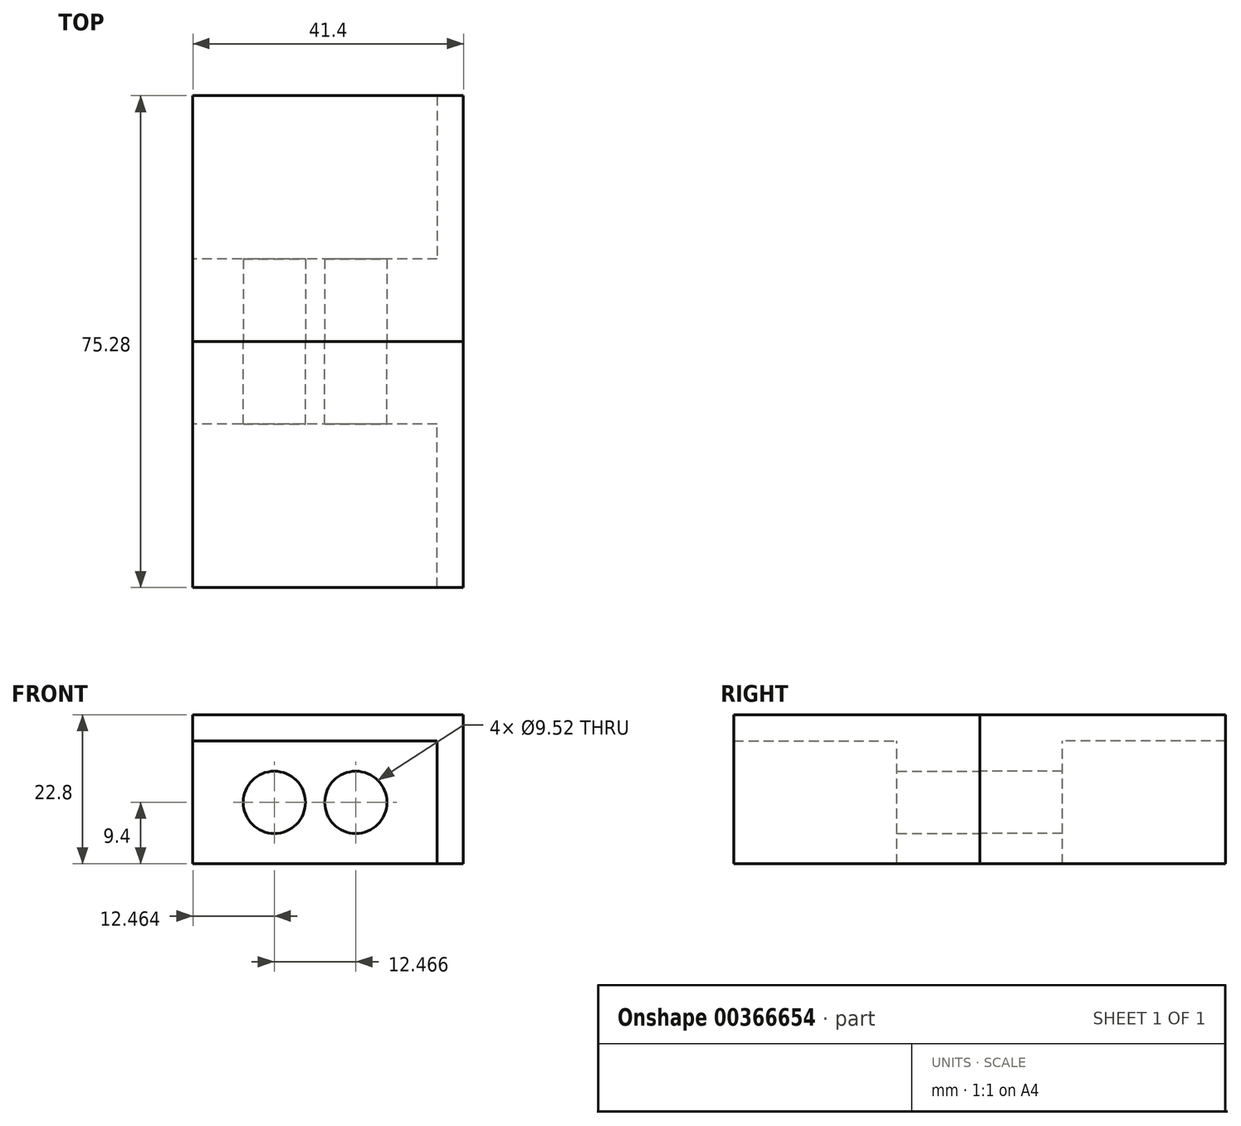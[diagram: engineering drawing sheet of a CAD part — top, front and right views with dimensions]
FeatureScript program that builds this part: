
annotation { "Feature Type Name" : "Feature", "Feature Type Description" : "" }
export const myFeature = defineFeature(function(context is Context, id is Id, definition is map)
    precondition{}
    {
        {
            var Q0;
            Q0=qCreatedBy(makeId("Front.planeOp"),FACE);
            var sketch = newSketch(context, id + "F0", { "sketchPlane" : qUnion([Q0])});
            skCircle(sketch, "E0", {"center": v(0, 0) * mm, "radius": 4.76 * mm});
            skLineSegment(sketch, "E1.bottom", {"start": v(12.47, -9.4) * mm, "end": v(-24.93, -9.4) * mm});
            skLineSegment(sketch, "E1.top", {"start": v(12.47, 9.4) * mm, "end": v(-24.93, 9.4) * mm});
            skLineSegment(sketch, "E1.left", {"start": v(12.47, -9.4) * mm, "end": v(12.47, 9.4) * mm});
            skLineSegment(sketch, "E1.right", {"start": v(-24.93, -9.4) * mm, "end": v(-24.93, 9.4) * mm});
            skCircle(sketch, "E2", {"center": v(-12.47, 0) * mm, "radius": 4.76 * mm});
            skSolve(sketch);
        }
        {
            var Q0;
            Q0=makeQuery(id+"F0.imprint","IMPRINT",FACE,{"disambiguationData":[TD([[makeQuery(id+"F0.imprint","IMPRINT",EDGE,{"derivedFrom":sQuery(id+"F0.wireOp",EDGE,"E0")}),-1.0]])]});
            extrude(context, id + "F1", {"entities" : qUnion([Q0]), "depth" : 12.64 * mm});
        }
        {
            var Q0;
            Q0=makeQuery(id+"F1.opExtrude","CAP_FACE",FACE,{"disambiguationData":[OSD([sQuery(id+"F0.wireOp",EDGE,"E0"),sQuery(id+"F0.wireOp",EDGE,"E1.bottom"),sQuery(id+"F0.wireOp",EDGE,"E1.top"),sQuery(id+"F0.wireOp",EDGE,"E1.left"),sQuery(id+"F0.wireOp",EDGE,"E1.right"),sQuery(id+"F0.wireOp",EDGE,"E2")])],"isStart":false});
            var sketch = newSketch(context, id + "F2", { "sketchPlane" : qUnion([Q0])});
            skLineSegment(sketch, "E3.0", {"start": v(12.47, -9.4) * mm, "end": v(12.47, 9.4) * mm});
            skLineSegment(sketch, "E3.1", {"start": v(12.47, 9.4) * mm, "end": v(-24.93, 9.4) * mm});
            skLineSegment(sketch, "E4", {"start": v(-24.93, 9.4) * mm, "end": v(-24.93, 13.4) * mm});
            skLineSegment(sketch, "E5", {"start": v(-24.93, 13.4) * mm, "end": v(16.47, 13.4) * mm});
            skLineSegment(sketch, "E6", {"start": v(16.47, 13.4) * mm, "end": v(16.47, -9.4) * mm});
            skLineSegment(sketch, "E7", {"start": v(12.47, -9.4) * mm, "end": v(16.47, -9.4) * mm});
            skSolve(sketch);
        }
        {
            var Q0;
            Q0 = qSketchRegion(id + "F2", true);
            var Q1;
            Q1=makeQuery(id+"F1.opExtrude","CAP_FACE",FACE,{"disambiguationData":[OSD([sQuery(id+"F0.wireOp",EDGE,"E0"),sQuery(id+"F0.wireOp",EDGE,"E1.bottom"),sQuery(id+"F0.wireOp",EDGE,"E1.top"),sQuery(id+"F0.wireOp",EDGE,"E1.left"),sQuery(id+"F0.wireOp",EDGE,"E1.right"),sQuery(id+"F0.wireOp",EDGE,"E2")])],"isStart":true});
            extrude(context, id + "F3", {"entities" : qUnion([Q0]), "operationType" : NewBodyOperationType.ADD, "depth" : 25 * mm, "hasSecondDirection" : true, "secondDirectionBound" : SecondDirectionBoundingType.UP_TO_SURFACE, "secondDirectionOppositeDirection" : true, "secondDirectionBoundEntityFace" : qUnion([Q1]), "secondDirectionDepth" : 37.6 * mm});
        }
        {
            var Q0;
            Q0=makeQuery(id+"F1.opExtrude","SWEPT_BODY",BODY,{"disambiguationData":[OSD([sQuery(id+"F0.wireOp",EDGE,"E0"),sQuery(id+"F0.wireOp",EDGE,"E1.bottom"),sQuery(id+"F0.wireOp",EDGE,"E1.top"),sQuery(id+"F0.wireOp",EDGE,"E1.left"),sQuery(id+"F0.wireOp",EDGE,"E1.right"),sQuery(id+"F0.wireOp",EDGE,"E2")])]});
            var Q1;
            Q1=qCreatedBy(makeId("Front.planeOp"),FACE);
            mirror(context, id + "F4", {"entities" : qUnion([Q0]), "mirrorPlane" : qUnion([Q1])});
        }
    });
